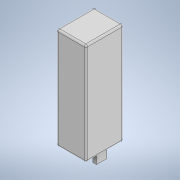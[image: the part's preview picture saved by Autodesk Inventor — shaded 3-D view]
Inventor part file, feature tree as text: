
AUTODESK INVENTOR PART (.ipt)
format: ipt  version: 2020 (Build 240168000, 168)  size: 125,440 bytes
history: native  units: mm
features: extrude x2, sketch x2, fillet x1
ambient origin geometry x8: Origin, YZ Plane, XZ Plane, XY Plane, X Axis, Y Axis, Z Axis, Center Point
bodies: Solid1 (feature_tree)
feature tree (5):
  extrude  "Extrusion1"  Depth=33.5mm
  fillet  "Fillet1"  Radius=43.0mm
  extrude  "Extrusion2"  Depth=10.0mm TaperAngle=0.0deg
  sketch  "Sketch1"  dims[d0=115.0mm d1=33.5mm d2=43.0mm d3=0.0mm]
  sketch  "Sketch2"  dims[d4=2.0mm d5=10.0mm d6=0.0mm]
